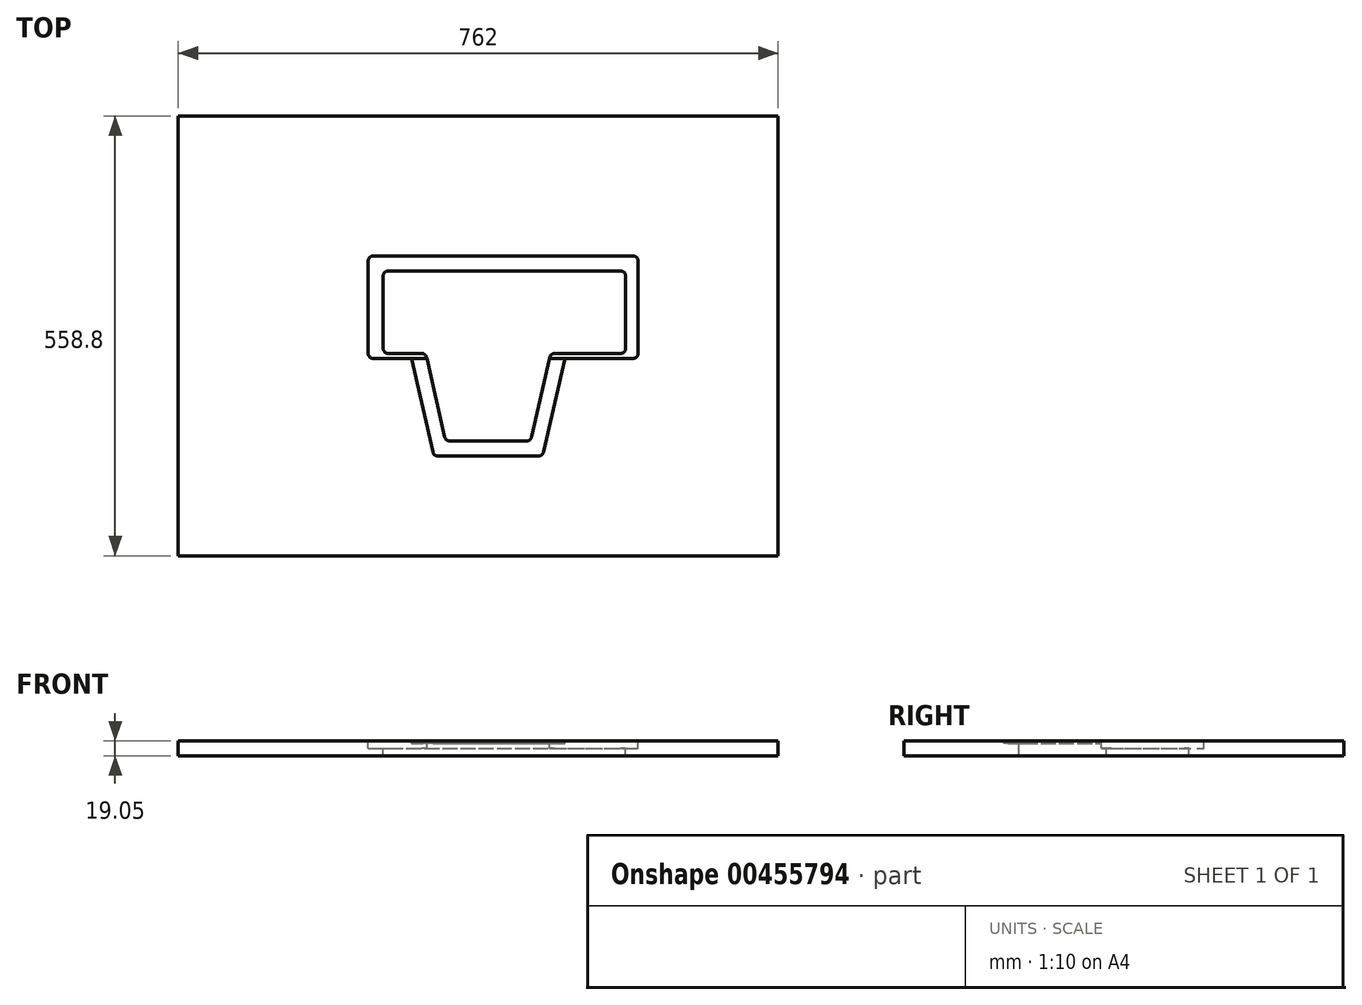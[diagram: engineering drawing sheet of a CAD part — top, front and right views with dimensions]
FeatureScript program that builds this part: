
annotation { "Feature Type Name" : "Feature", "Feature Type Description" : "" }
export const myFeature = defineFeature(function(context is Context, id is Id, definition is map)
    precondition{}
    {
        {
            var Q0;
            Q0=qCreatedBy(makeId("Top.planeOp"),FACE);
            var sketch = newSketch(context, id + "F0", { "sketchPlane" : qUnion([Q0])});
            skPoint(sketch, "E0.middle", {"position": v(0, 0) * mm});
            skLineSegment(sketch, "E1.bottom", {"start": v(331.79, -355.6) * mm, "end": v(-430.21, -355.6) * mm});
            skLineSegment(sketch, "E1.top", {"start": v(331.79, 203.2) * mm, "end": v(-430.21, 203.2) * mm});
            skLineSegment(sketch, "E1.left", {"start": v(331.79, -355.6) * mm, "end": v(331.79, 203.2) * mm});
            skLineSegment(sketch, "E1.right", {"start": v(-430.21, -355.6) * mm, "end": v(-430.21, 203.2) * mm});
            skSolve(sketch);
        }
        {
            var Q0;
            Q0=makeQuery(id+"F0.imprint","IMPRINT",FACE,{"disambiguationData":[TD([[makeQuery(id+"F0.imprint","IMPRINT",EDGE,{"derivedFrom":sQuery(id+"F0.wireOp",EDGE,"E1.bottom")}),-1.0]])]});
            var sketch = newSketch(context, id + "F1", { "sketchPlane" : qUnion([Q0])});
            skLineSegment(sketch, "E2.bottom", {"start": v(-188.91, -104.77) * mm, "end": v(-114.44, -104.77) * mm});
            skLineSegment(sketch, "E2.top", {"start": v(-188.91, 25.4) * mm, "end": v(153.99, 25.4) * mm});
            skLineSegment(sketch, "E2.left", {"start": v(-188.91, -104.78) * mm, "end": v(-188.91, 25.4) * mm});
            skLineSegment(sketch, "E2.right", {"start": v(153.99, -104.77) * mm, "end": v(153.99, 25.4) * mm});
            skLineSegment(sketch, "E3.0", {"start": v(-169.86, 6.35) * mm, "end": v(138.11, 6.35) * mm});
            skLineSegment(sketch, "E4.0", {"start": v(-169.86, -98.43) * mm, "end": v(-169.86, 6.35) * mm});
            skLineSegment(sketch, "E5.0", {"start": v(-169.86, -98.42) * mm, "end": v(-115.89, -98.42) * mm});
            skLineSegment(sketch, "E6.0", {"start": v(138.11, -98.42) * mm, "end": v(138.11, 6.35) * mm});
            skLineSegment(sketch, "E7", {"start": v(-90.49, -209.55) * mm, "end": v(-115.89, -98.42) * mm});
            skLineSegment(sketch, "E8.trimOffspring", {"start": v(42.86, -98.42) * mm, "end": v(138.11, -98.42) * mm});
            skLineSegment(sketch, "E9", {"start": v(-90.49, -209.55) * mm, "end": v(17.46, -209.55) * mm});
            skLineSegment(sketch, "E10", {"start": v(17.46, -209.55) * mm, "end": v(42.86, -98.42) * mm});
            skLineSegment(sketch, "E11.0", {"start": v(32.65, -228.6) * mm, "end": v(62.4, -98.43) * mm});
            skLineSegment(sketch, "E11.1", {"start": v(-105.67, -228.6) * mm, "end": v(32.65, -228.6) * mm});
            skLineSegment(sketch, "E11.2", {"start": v(-105.67, -228.6) * mm, "end": v(-135.43, -98.42) * mm});
            skLineSegment(sketch, "E12.trimOffspring", {"start": v(41.41, -104.77) * mm, "end": v(153.99, -104.77) * mm});
            skSolve(sketch);
        }
        {
            var Q0;
            Q0 = qSketchRegion(id + "F0", true);
            extrude(context, id + "F2", {"entities" : qUnion([Q0]), "oppositeDirection" : true, "depth" : 19.05 * mm});
        }
        {
            var Q0;
            Q0=makeQuery(id+"F1.imprint","IMPRINT",FACE,{"disambiguationData":[TD([[makeQuery(id+"F1.imprint","IMPRINT",EDGE,{"derivedFrom":sQuery(id+"F1.wireOp",EDGE,"E3.0")}),-1.0]])]});
            var Q1;
            {var subQ5=sQuery(id+"F1.wireOp",EDGE,"E9");Q1=makeQuery(id+"F1.imprint","IMPRINT",FACE,{"disambiguationData":[TD([[makeQuery(id+"F1.imprint","IMPRINT",EDGE,{"derivedFrom":subQ5}),1.0]])]});}
            extrude(context, id + "F3", {"entities" : qUnion([Q0, Q1]), "operationType" : NewBodyOperationType.REMOVE, "oppositeDirection" : true, "depth" : 25.4 * mm});
        }
        {
            var Q0;
            Q0=makeQuery(id+"F1.imprint","IMPRINT",FACE,{"disambiguationData":[TD([[makeQuery(id+"F1.imprint","IMPRINT",EDGE,{"derivedFrom":sQuery(id+"F1.wireOp",EDGE,"E2.top")}),-1.0]])]});
            extrude(context, id + "F4", {"entities" : qUnion([Q0]), "operationType" : NewBodyOperationType.REMOVE, "oppositeDirection" : true, "depth" : 9.52 * mm});
        }
        {
            var Q0;
            {var subQ0=sQuery(id+"F1.wireOp",EDGE,"E10");var subQ1=sQuery(id+"F1.wireOp",EDGE,"E8.trimOffspring");var subQ2=makeQuery(id+"F1.imprint","INTERSECT",VERTEX,{"derivedFrom":[subQ1,subQ0]});Q0=makeQuery(id+"F1.imprint","IMPRINT",FACE,{"disambiguationData":[TD([[makeQuery(id+"F1.imprint","IMPRINT",EDGE,{"disambiguationData":[TD([[subQ2,-1.0]])],"derivedFrom":subQ1}),-1.0]])]});}
            extrude(context, id + "F5", {"entities" : qUnion([Q0]), "operationType" : NewBodyOperationType.REMOVE, "oppositeDirection" : true, "depth" : 9.52 * mm});
        }
        {
            var Q0;
            {var subQ0=sQuery(id+"F1.wireOp",EDGE,"E7");var subQ1=sQuery(id+"F1.wireOp",EDGE,"E2.bottom");var subQ2=makeQuery(id+"F1.imprint","INTERSECT",VERTEX,{"derivedFrom":[subQ1,subQ0]});Q0=makeQuery(id+"F1.imprint","IMPRINT",FACE,{"disambiguationData":[TD([[makeQuery(id+"F1.imprint","IMPRINT",EDGE,{"disambiguationData":[TD([[subQ2,1.0]])],"derivedFrom":subQ1}),1.0]])]});}
            extrude(context, id + "F6", {"entities" : qUnion([Q0]), "operationType" : NewBodyOperationType.REMOVE, "oppositeDirection" : true, "depth" : 9.52 * mm});
        }
        {
            var Q0;
            {var subQ0=sQuery(id+"F1.wireOp",EDGE,"E9");Q0=makeQuery(id+"F1.imprint","IMPRINT",FACE,{"disambiguationData":[TD([[makeQuery(id+"F1.imprint","IMPRINT",EDGE,{"derivedFrom":subQ0}),-1.0]])]});}
            extrude(context, id + "F7", {"entities" : qUnion([Q0]), "operationType" : NewBodyOperationType.REMOVE, "oppositeDirection" : true, "depth" : 3.17 * mm});
        }
        {
            var Q0;
            Q0=makeQuery(id+"F3.boolean.opBoolean","COPY",EDGE,{"derivedFrom":makeQuery(id+"F3.opExtrude","SWEPT_EDGE",EDGE,{"disambiguationData":[OSD([sQuery(id+"F1.wireOp",EDGE,"E3.0"),sQuery(id+"F1.wireOp",EDGE,"E4.0")])]})});
            var Q1;
            Q1=makeQuery(id+"F3.boolean.opBoolean","COPY",EDGE,{"derivedFrom":makeQuery(id+"F3.opExtrude","SWEPT_EDGE",EDGE,{"disambiguationData":[OSD([sQuery(id+"F1.wireOp",EDGE,"E4.0"),sQuery(id+"F1.wireOp",EDGE,"E5.0")])]})});
            var Q2;
            Q2=makeQuery(id+"F3.boolean.opBoolean","COPY",EDGE,{"derivedFrom":makeQuery(id+"F3.opExtrude","SWEPT_EDGE",EDGE,{"disambiguationData":[OSD([sQuery(id+"F1.wireOp",EDGE,"E5.0"),sQuery(id+"F1.wireOp",EDGE,"E7")])]})});
            var Q3;
            Q3=makeQuery(id+"F3.boolean.opBoolean","COPY",EDGE,{"derivedFrom":makeQuery(id+"F3.opExtrude","SWEPT_EDGE",EDGE,{"disambiguationData":[OSD([sQuery(id+"F1.wireOp",EDGE,"E7"),sQuery(id+"F1.wireOp",EDGE,"E9")])]})});
            var Q4;
            Q4=makeQuery(id+"F3.boolean.opBoolean","COPY",EDGE,{"derivedFrom":makeQuery(id+"F3.opExtrude","SWEPT_EDGE",EDGE,{"disambiguationData":[OSD([sQuery(id+"F1.wireOp",EDGE,"E9"),sQuery(id+"F1.wireOp",EDGE,"E10")])]})});
            var Q5;
            Q5=makeQuery(id+"F3.boolean.opBoolean","COPY",EDGE,{"derivedFrom":makeQuery(id+"F3.opExtrude","SWEPT_EDGE",EDGE,{"disambiguationData":[OSD([sQuery(id+"F1.wireOp",EDGE,"E8.trimOffspring"),sQuery(id+"F1.wireOp",EDGE,"E10")])]})});
            var Q6;
            Q6=makeQuery(id+"F3.boolean.opBoolean","COPY",EDGE,{"derivedFrom":makeQuery(id+"F3.opExtrude","SWEPT_EDGE",EDGE,{"disambiguationData":[OSD([sQuery(id+"F1.wireOp",EDGE,"E6.0"),sQuery(id+"F1.wireOp",EDGE,"E8.trimOffspring")])]})});
            var Q7;
            Q7=makeQuery(id+"F3.boolean.opBoolean","COPY",EDGE,{"derivedFrom":makeQuery(id+"F3.opExtrude","SWEPT_EDGE",EDGE,{"disambiguationData":[OSD([sQuery(id+"F1.wireOp",EDGE,"E3.0"),sQuery(id+"F1.wireOp",EDGE,"E6.0")])]})});
            fillet(context, id + "F8", {"entities" : qUnion([Q0, Q1, Q2, Q3, Q4, Q5, Q6, Q7]), "radius" : 6.35 * mm, "tangentPropagation" : true, "allowEdgeOverflow" : false});
        }
        {
            var Q0;
            Q0=makeQuery(id+"F4.boolean.opBoolean","COPY",EDGE,{"derivedFrom":makeQuery(id+"F4.opExtrude","SWEPT_EDGE",EDGE,{"disambiguationData":[OSD([sQuery(id+"F1.wireOp",EDGE,"E2.top"),sQuery(id+"F1.wireOp",EDGE,"E2.left")])]})});
            var Q1;
            Q1=makeQuery(id+"F4.boolean.opBoolean","COPY",EDGE,{"derivedFrom":makeQuery(id+"F4.opExtrude","SWEPT_EDGE",EDGE,{"disambiguationData":[OSD([sQuery(id+"F1.wireOp",EDGE,"E2.top"),sQuery(id+"F1.wireOp",EDGE,"E2.right")])]})});
            var Q2;
            Q2=makeQuery(id+"F4.boolean.opBoolean","COPY",EDGE,{"derivedFrom":makeQuery(id+"F4.opExtrude","SWEPT_EDGE",EDGE,{"disambiguationData":[OSD([sQuery(id+"F1.wireOp",EDGE,"E2.right"),sQuery(id+"F1.wireOp",EDGE,"E12.trimOffspring")])]})});
            var Q3;
            Q3=makeQuery(id+"F7.boolean.opBoolean","COPY",EDGE,{"derivedFrom":makeQuery(id+"F7.opExtrude","SWEPT_EDGE",EDGE,{"disambiguationData":[OSD([sQuery(id+"F1.wireOp",EDGE,"E11.0"),sQuery(id+"F1.wireOp",EDGE,"E11.1")])]})});
            var Q4;
            Q4=makeQuery(id+"F7.boolean.opBoolean","COPY",EDGE,{"derivedFrom":makeQuery(id+"F7.opExtrude","SWEPT_EDGE",EDGE,{"disambiguationData":[OSD([sQuery(id+"F1.wireOp",EDGE,"E11.1"),sQuery(id+"F1.wireOp",EDGE,"E11.2")])]})});
            var Q5;
            Q5=makeQuery(id+"F4.boolean.opBoolean","COPY",EDGE,{"derivedFrom":makeQuery(id+"F4.opExtrude","SWEPT_EDGE",EDGE,{"disambiguationData":[OSD([sQuery(id+"F1.wireOp",EDGE,"E2.bottom"),sQuery(id+"F1.wireOp",EDGE,"E2.left")])]})});
            fillet(context, id + "F9", {"entities" : qUnion([Q0, Q1, Q2, Q3, Q4, Q5]), "radius" : 6.35 * mm, "tangentPropagation" : true, "allowEdgeOverflow" : false});
        }
    });
